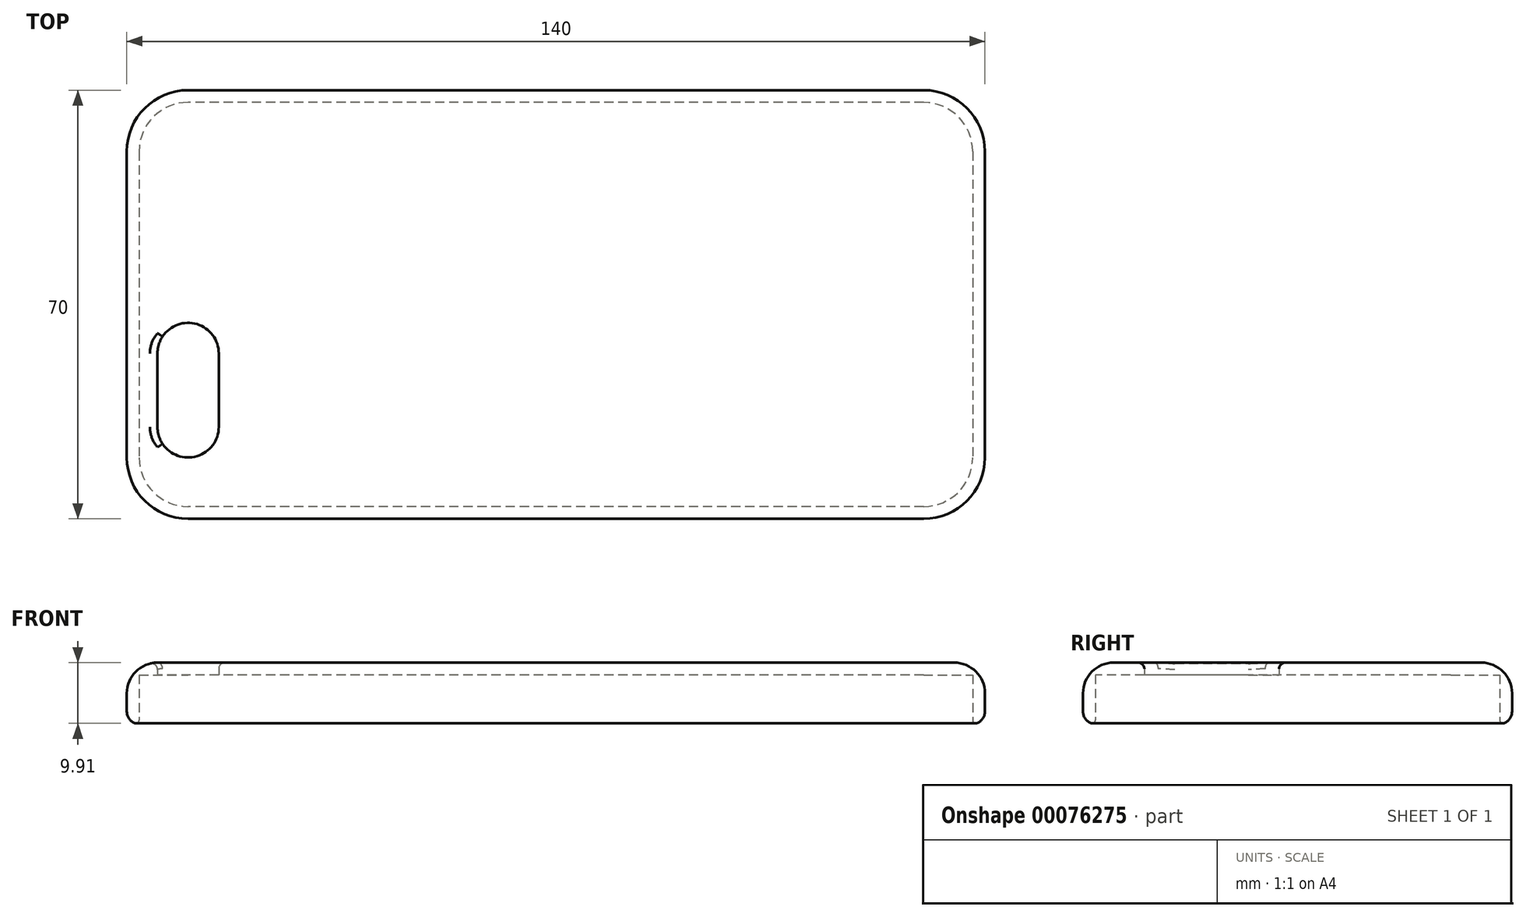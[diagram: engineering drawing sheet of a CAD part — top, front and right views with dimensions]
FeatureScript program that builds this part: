
annotation { "Feature Type Name" : "Feature", "Feature Type Description" : "" }
export const myFeature = defineFeature(function(context is Context, id is Id, definition is map)
    precondition{}
    {
        {
            var Q0;
            Q0=qCreatedBy(makeId("Top.planeOp"),FACE);
            var sketch = newSketch(context, id + "F0", { "sketchPlane" : qUnion([Q0])});
            skLineSegment(sketch, "E0.bottom", {"start": v(60, 35) * mm, "end": v(-60, 35) * mm});
            skLineSegment(sketch, "E0.top", {"start": v(60, -35) * mm, "end": v(-60, -35) * mm});
            skLineSegment(sketch, "E0.left", {"start": v(70, 25) * mm, "end": v(70, -25) * mm});
            skLineSegment(sketch, "E0.right", {"start": v(-70, 25) * mm, "end": v(-70, -25) * mm});
            skPoint(sketch, "E0.middle", {"position": v(0, 0) * mm});
            skPoint(sketch, "E1.visualSharp", {"position": v(-70, 35) * mm});
            skArc(sketch, "E1.filletArc", {"start": v(-60, 35) * mm, "mid": v(-67.07, 32.07) * mm, "end": v(-70, 25) * mm});
            skPoint(sketch, "E2.visualSharp", {"position": v(-70, -35) * mm});
            skArc(sketch, "E2.filletArc", {"start": v(-70, -25) * mm, "mid": v(-67.07, -32.07) * mm, "end": v(-60, -35) * mm});
            skPoint(sketch, "E3.visualSharp", {"position": v(70, -35) * mm});
            skArc(sketch, "E3.filletArc", {"start": v(60, -35) * mm, "mid": v(67.07, -32.07) * mm, "end": v(70, -25) * mm});
            skPoint(sketch, "E4.visualSharp", {"position": v(70, 35) * mm});
            skArc(sketch, "E4.filletArc", {"start": v(70, 25) * mm, "mid": v(67.07, 32.07) * mm, "end": v(60, 35) * mm});
            skLineSegment(sketch, "E5.0", {"start": v(-65, -8) * mm, "end": v(-65, -20) * mm});
            skLineSegment(sketch, "E6.0", {"start": v(-60, -25) * mm, "end": v(-60, -25) * mm});
            skLineSegment(sketch, "E7.0", {"start": v(-55, -8) * mm, "end": v(-55, -20) * mm});
            skLineSegment(sketch, "E8", {"start": v(-60, -3) * mm, "end": v(-60, -3) * mm});
            skArc(sketch, "E9.filletArc", {"start": v(-55, -8) * mm, "mid": v(-56.46, -4.46) * mm, "end": v(-60, -3) * mm});
            skArc(sketch, "E10.filletArc", {"start": v(-60, -3) * mm, "mid": v(-63.54, -4.46) * mm, "end": v(-65, -8) * mm});
            skArc(sketch, "E11.filletArc", {"start": v(-65, -20) * mm, "mid": v(-63.54, -23.54) * mm, "end": v(-60, -25) * mm});
            skArc(sketch, "E12.filletArc", {"start": v(-60, -25) * mm, "mid": v(-56.46, -23.54) * mm, "end": v(-55, -20) * mm});
            skSolve(sketch);
        }
        {
            var Q0;
            Q0 = qSketchRegion(id + "F0", true);
            extrude(context, id + "F1", {"entities" : qUnion([Q0]), "depth" : 10 * mm});
        }
        {
            var Q0;
            Q0=makeQuery(id+"F1.opExtrude","SWEPT_FACE",FACE,{"disambiguationData":[OSD([sQuery(id+"F0.wireOp",EDGE,"E11.filletArc"),sQuery(id+"F0.wireOp",EDGE,"E12.filletArc")])]});
            var Q1;
            Q1=makeQuery(id+"F1.opExtrude","SWEPT_FACE",FACE,{"disambiguationData":[OSD([sQuery(id+"F0.wireOp",EDGE,"E5.0")])]});
            var Q2;
            Q2=makeQuery(id+"F1.opExtrude","SWEPT_FACE",FACE,{"disambiguationData":[OSD([sQuery(id+"F0.wireOp",EDGE,"E9.filletArc"),sQuery(id+"F0.wireOp",EDGE,"E10.filletArc")])]});
            var Q3;
            Q3=makeQuery(id+"F1.opExtrude","CAP_FACE",FACE,{"disambiguationData":[OSD([sQuery(id+"F0.wireOp",EDGE,"E0.bottom"),sQuery(id+"F0.wireOp",EDGE,"E0.top"),sQuery(id+"F0.wireOp",EDGE,"E0.left"),sQuery(id+"F0.wireOp",EDGE,"E0.right"),sQuery(id+"F0.wireOp",EDGE,"E1.filletArc"),sQuery(id+"F0.wireOp",EDGE,"E2.filletArc"),sQuery(id+"F0.wireOp",EDGE,"E3.filletArc"),sQuery(id+"F0.wireOp",EDGE,"E4.filletArc"),sQuery(id+"F0.wireOp",EDGE,"E5.0"),sQuery(id+"F0.wireOp",EDGE,"E7.0"),sQuery(id+"F0.wireOp",EDGE,"E9.filletArc"),sQuery(id+"F0.wireOp",EDGE,"E10.filletArc"),sQuery(id+"F0.wireOp",EDGE,"E11.filletArc"),sQuery(id+"F0.wireOp",EDGE,"E12.filletArc")])],"isStart":true});
            var Q4;
            Q4=makeQuery(id+"F1.opExtrude","SWEPT_FACE",FACE,{"disambiguationData":[OSD([sQuery(id+"F0.wireOp",EDGE,"E7.0")])]});
            shell(context, id + "F2", {"entities" : qUnion([Q0, Q1, Q2, Q3, Q4]), "thickness" : 2 * mm});
        }
        {
            var Q0;
            Q0=makeQuery(id+"F1.opExtrude","CAP_EDGE",EDGE,{"disambiguationData":[OSD([sQuery(id+"F0.wireOp",EDGE,"E0.top")])],"isStart":false});
            var Q1;
            Q1=makeQuery(id+"F1.opExtrude","CAP_EDGE",EDGE,{"disambiguationData":[OSD([sQuery(id+"F0.wireOp",EDGE,"E2.filletArc")])],"isStart":false});
            var Q2;
            Q2=makeQuery(id+"F1.opExtrude","CAP_EDGE",EDGE,{"disambiguationData":[OSD([sQuery(id+"F0.wireOp",EDGE,"E0.right")])],"isStart":false});
            var Q3;
            Q3=makeQuery(id+"F1.opExtrude","CAP_EDGE",EDGE,{"disambiguationData":[OSD([sQuery(id+"F0.wireOp",EDGE,"E1.filletArc")])],"isStart":false});
            var Q4;
            Q4=makeQuery(id+"F1.opExtrude","CAP_EDGE",EDGE,{"disambiguationData":[OSD([sQuery(id+"F0.wireOp",EDGE,"E0.bottom")])],"isStart":false});
            var Q5;
            Q5=makeQuery(id+"F1.opExtrude","CAP_EDGE",EDGE,{"disambiguationData":[OSD([sQuery(id+"F0.wireOp",EDGE,"E4.filletArc")])],"isStart":false});
            var Q6;
            Q6=makeQuery(id+"F1.opExtrude","CAP_EDGE",EDGE,{"disambiguationData":[OSD([sQuery(id+"F0.wireOp",EDGE,"E0.left")])],"isStart":false});
            var Q7;
            Q7=makeQuery(id+"F1.opExtrude","CAP_EDGE",EDGE,{"disambiguationData":[OSD([sQuery(id+"F0.wireOp",EDGE,"E3.filletArc")])],"isStart":false});
            fillet(context, id + "F3", {"entities" : qUnion([Q0, Q1, Q2, Q3, Q4, Q5, Q6, Q7]), "radius" : 5 * mm, "tangentPropagation" : true, "allowEdgeOverflow" : false});
        }
        {
            var Q0;
            Q0=makeQuery(id+"F1.opExtrude","CAP_EDGE",EDGE,{"disambiguationData":[OSD([sQuery(id+"F0.wireOp",EDGE,"E0.top")])],"isStart":true});
            fillet(context, id + "F4", {"entities" : qUnion([Q0]), "radius" : 2 * mm, "tangentPropagation" : true, "allowEdgeOverflow" : false});
        }
        {
            var Q0;
            Q0=makeQuery(id+"F1.opExtrude","CAP_EDGE",EDGE,{"disambiguationData":[OSD([sQuery(id+"F0.wireOp",EDGE,"E11.filletArc"),sQuery(id+"F0.wireOp",EDGE,"E12.filletArc")])],"isStart":false});
            fillet(context, id + "F5", {"entities" : qUnion([Q0]), "radius" : 1 * mm, "tangentPropagation" : true, "allowEdgeOverflow" : false});
        }
        {
            var Q0;
            {var subQ0=sQuery(id+"F0.wireOp",EDGE,"E0.top");Q0=makeQuery(id+"F4.opFillet","BLEND_EDGE",EDGE,{"blendedFrom":[makeQuery(id+"F1.opExtrude","CAP_EDGE",EDGE,{"disambiguationData":[OSD([subQ0])],"isStart":true}),makeQuery(id+"F2.opShell","OFFSET_FACE",FACE,{"disambiguationData":[OSD([subQ0])]})],"blendedInto":[makeQuery(id+"F2.opShell","OFFSET_FACE",FACE,{"disambiguationData":[OSD([subQ0])]})]});}
            fillet(context, id + "F6", {"entities" : qUnion([Q0]), "radius" : 0.5 * mm, "tangentPropagation" : true, "allowEdgeOverflow" : false});
        }
    });
